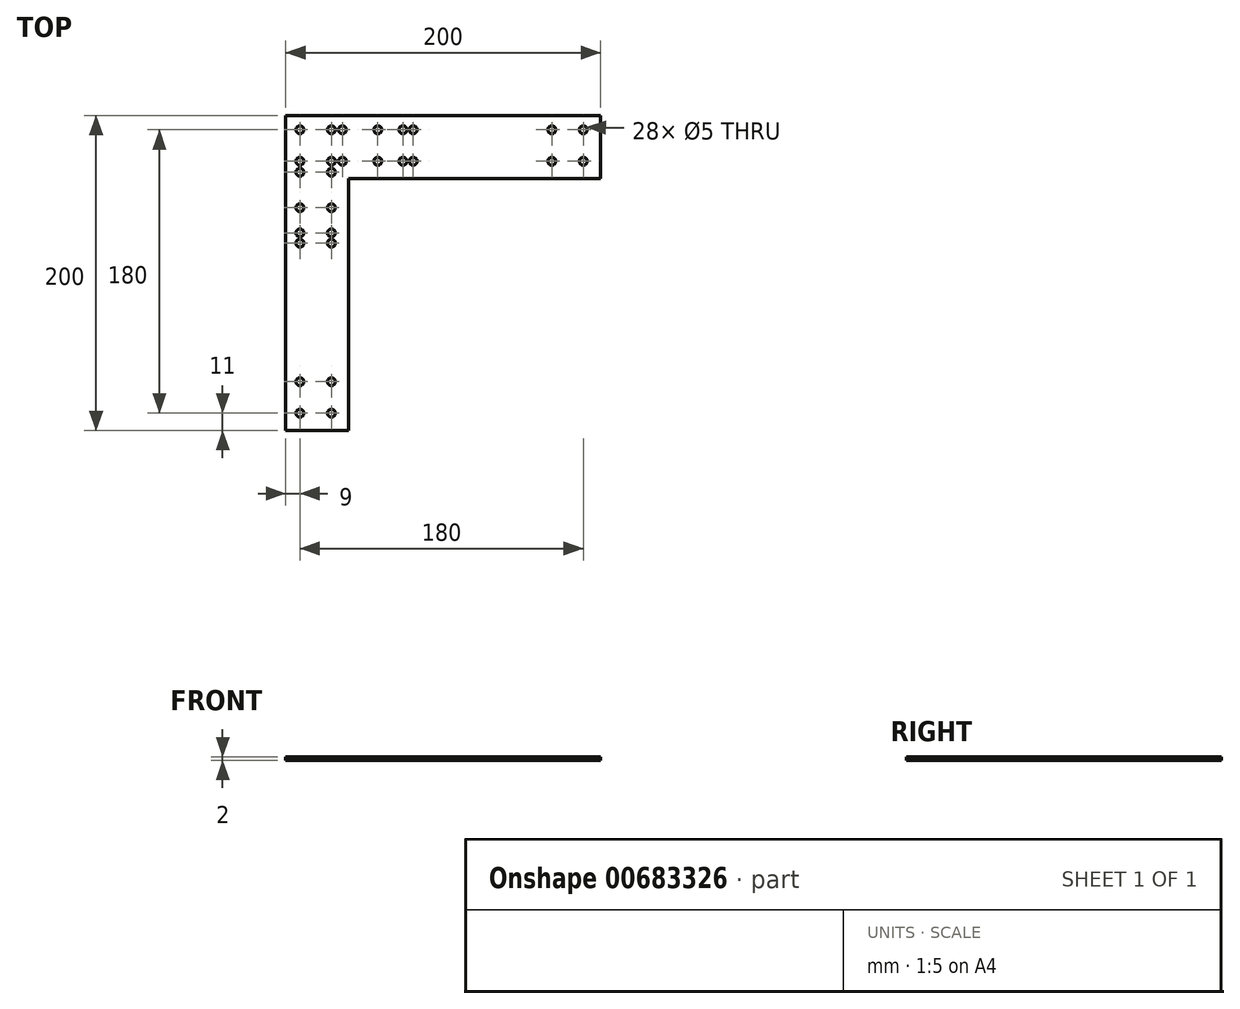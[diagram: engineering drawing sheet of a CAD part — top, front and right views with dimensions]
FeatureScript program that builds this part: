
annotation { "Feature Type Name" : "Feature", "Feature Type Description" : "" }
export const myFeature = defineFeature(function(context is Context, id is Id, definition is map)
    precondition{}
    {
        {
            var Q0;
            Q0=qCreatedBy(makeId("Top.planeOp"),FACE);
            var sketch = newSketch(context, id + "F0", { "sketchPlane" : qUnion([Q0])});
            skLineSegment(sketch, "E0", {"start": v(0, 0) * mm, "end": v(200, 0) * mm});
            skLineSegment(sketch, "E1", {"start": v(0, 0) * mm, "end": v(0, -200) * mm});
            skLineSegment(sketch, "E2.bottom", {"start": v(0, 0) * mm, "end": v(9, 0) * mm, "construction": true});
            skLineSegment(sketch, "E2.top", {"start": v(0, -9) * mm, "end": v(9, -9) * mm, "construction": true});
            skLineSegment(sketch, "E2.left", {"start": v(0, 0) * mm, "end": v(0, -9) * mm, "construction": true});
            skLineSegment(sketch, "E2.right", {"start": v(9, 0) * mm, "end": v(9, -9) * mm, "construction": true});
            skCircle(sketch, "E3", {"center": v(9, -9) * mm, "radius": 2.5 * mm});
            skLineSegment(sketch, "E4.bottom", {"start": v(9, -9) * mm, "end": v(29, -9) * mm, "construction": true});
            skLineSegment(sketch, "E4.top", {"start": v(9, -29) * mm, "end": v(29, -29) * mm, "construction": true});
            skLineSegment(sketch, "E4.left", {"start": v(9, -9) * mm, "end": v(9, -29) * mm, "construction": true});
            skLineSegment(sketch, "E4.right", {"start": v(29, -9) * mm, "end": v(29, -29) * mm, "construction": true});
            skLineSegment(sketch, "E5", {"start": v(29, -9) * mm, "end": v(169, -9) * mm, "construction": true});
            skLineSegment(sketch, "E6", {"start": v(9, -29) * mm, "end": v(9, -169) * mm, "construction": true});
            skLineSegment(sketch, "E7.bottom", {"start": v(9, -169) * mm, "end": v(29, -169) * mm, "construction": true});
            skLineSegment(sketch, "E7.top", {"start": v(9, -189) * mm, "end": v(29, -189) * mm, "construction": true});
            skLineSegment(sketch, "E7.left", {"start": v(9, -169) * mm, "end": v(9, -189) * mm, "construction": true});
            skLineSegment(sketch, "E7.right", {"start": v(29, -169) * mm, "end": v(29, -189) * mm, "construction": true});
            skLineSegment(sketch, "E8.bottom", {"start": v(169, -9) * mm, "end": v(189, -9) * mm, "construction": true});
            skLineSegment(sketch, "E8.top", {"start": v(169, -29) * mm, "end": v(189, -29) * mm, "construction": true});
            skLineSegment(sketch, "E8.left", {"start": v(169, -9) * mm, "end": v(169, -29) * mm, "construction": true});
            skLineSegment(sketch, "E8.right", {"start": v(189, -9) * mm, "end": v(189, -29) * mm, "construction": true});
            skCircle(sketch, "E9", {"center": v(169, -9) * mm, "radius": 2.5 * mm});
            skCircle(sketch, "E10", {"center": v(169, -29) * mm, "radius": 2.5 * mm});
            skCircle(sketch, "E11", {"center": v(189, -9) * mm, "radius": 2.5 * mm});
            skCircle(sketch, "E12", {"center": v(189, -29) * mm, "radius": 2.5 * mm});
            skCircle(sketch, "E13", {"center": v(29, -29) * mm, "radius": 2.5 * mm});
            skCircle(sketch, "E14", {"center": v(29, -9) * mm, "radius": 2.5 * mm});
            skCircle(sketch, "E15", {"center": v(9, -29) * mm, "radius": 2.5 * mm});
            skCircle(sketch, "E16", {"center": v(9, -169) * mm, "radius": 2.5 * mm});
            skCircle(sketch, "E17", {"center": v(29, -169) * mm, "radius": 2.5 * mm});
            skCircle(sketch, "E18", {"center": v(29, -189) * mm, "radius": 2.5 * mm});
            skCircle(sketch, "E19", {"center": v(9, -189) * mm, "radius": 2.5 * mm});
            skLineSegment(sketch, "E20.top", {"start": v(0, -40) * mm, "end": v(200, -40) * mm});
            skLineSegment(sketch, "E20.left", {"start": v(0, 0) * mm, "end": v(0, -40) * mm});
            skLineSegment(sketch, "E20.right", {"start": v(200, 0) * mm, "end": v(200, -40) * mm});
            skLineSegment(sketch, "E21.bottom", {"start": v(0, 0) * mm, "end": v(40, 0) * mm});
            skLineSegment(sketch, "E21.top", {"start": v(0, -200) * mm, "end": v(40, -200) * mm});
            skLineSegment(sketch, "E21.right", {"start": v(40, 0) * mm, "end": v(40, -200) * mm});
            skLineSegment(sketch, "E22", {"start": v(29, -29) * mm, "end": v(58.5, -29) * mm});
            skLineSegment(sketch, "E23", {"start": v(29, -29) * mm, "end": v(74.5, -29) * mm});
            skLineSegment(sketch, "E24", {"start": v(58.5, -29) * mm, "end": v(58.5, -9) * mm});
            skLineSegment(sketch, "E25", {"start": v(74.5, -29) * mm, "end": v(74.5, -9) * mm});
            skCircle(sketch, "E26", {"center": v(58.5, -9) * mm, "radius": 2.5 * mm});
            skCircle(sketch, "E27", {"center": v(74.5, -9) * mm, "radius": 2.5 * mm});
            skCircle(sketch, "E28", {"center": v(74.5, -29) * mm, "radius": 2.5 * mm});
            skCircle(sketch, "E29", {"center": v(58.5, -29) * mm, "radius": 2.5 * mm});
            skLineSegment(sketch, "E30.bottom", {"start": v(81, -9) * mm, "end": v(36, -9) * mm});
            skLineSegment(sketch, "E30.top", {"start": v(81, -29) * mm, "end": v(36, -29) * mm});
            skLineSegment(sketch, "E30.left", {"start": v(81, -9) * mm, "end": v(81, -29) * mm});
            skLineSegment(sketch, "E30.right", {"start": v(36, -9) * mm, "end": v(36, -29) * mm});
            skPoint(sketch, "E30.middle", {"position": v(58.5, -19) * mm});
            skCircle(sketch, "E31", {"center": v(81, -9) * mm, "radius": 2.5 * mm});
            skCircle(sketch, "E32", {"center": v(81, -29) * mm, "radius": 2.5 * mm});
            skCircle(sketch, "E33", {"center": v(36, -29) * mm, "radius": 2.5 * mm});
            skCircle(sketch, "E34", {"center": v(36, -9) * mm, "radius": 2.5 * mm});
            skLineSegment(sketch, "E35", {"start": v(29, -29) * mm, "end": v(29, -58.5) * mm});
            skLineSegment(sketch, "E36", {"start": v(29, -29) * mm, "end": v(29, -74.5) * mm});
            skLineSegment(sketch, "E37", {"start": v(29, -58.5) * mm, "end": v(9, -58.5) * mm});
            skLineSegment(sketch, "E38", {"start": v(29, -74.5) * mm, "end": v(9, -74.5) * mm});
            skCircle(sketch, "E39", {"center": v(9, -58.5) * mm, "radius": 2.5 * mm});
            skCircle(sketch, "E40", {"center": v(29, -58.5) * mm, "radius": 2.5 * mm});
            skCircle(sketch, "E41", {"center": v(29, -74.5) * mm, "radius": 2.5 * mm});
            skCircle(sketch, "E42", {"center": v(9, -74.5) * mm, "radius": 2.5 * mm});
            skLineSegment(sketch, "E43.bottom", {"start": v(29, -36) * mm, "end": v(9, -36) * mm});
            skLineSegment(sketch, "E43.top", {"start": v(29, -81) * mm, "end": v(9, -81) * mm});
            skLineSegment(sketch, "E43.left", {"start": v(29, -36) * mm, "end": v(29, -81) * mm});
            skLineSegment(sketch, "E43.right", {"start": v(9, -36) * mm, "end": v(9, -81) * mm});
            skPoint(sketch, "E43.middle", {"position": v(19, -58.5) * mm});
            skCircle(sketch, "E44", {"center": v(9, -36) * mm, "radius": 2.5 * mm});
            skCircle(sketch, "E45", {"center": v(9, -81) * mm, "radius": 2.5 * mm});
            skCircle(sketch, "E46", {"center": v(29, -81) * mm, "radius": 2.5 * mm});
            skCircle(sketch, "E47", {"center": v(29, -36) * mm, "radius": 2.5 * mm});
            skSolve(sketch);
        }
        {
            var Q0;
            Q0 = qSketchRegion(id + "F0", true);
            var Q1;
            {var subQ6=sQuery(id+"F0.wireOp",EDGE,"E21.right");var subQ9=sQuery(id+"F0.wireOp",EDGE,"E30.bottom");var subQ10=makeQuery(id+"F0.imprint","INTERSECT",VERTEX,{"derivedFrom":[subQ6,subQ9]});Q1=makeQuery(id+"F0.imprint","IMPRINT",FACE,{"disambiguationData":[TD([[makeQuery(id+"F0.imprint","IMPRINT",EDGE,{"disambiguationData":[TD([[subQ10,-1.0]])],"derivedFrom":subQ6}),-1.0]])]});}
            var Q2;
            {var subQ3=sQuery(id+"F0.wireOp",EDGE,"E30.bottom");var subQ9=sQuery(id+"F0.wireOp",EDGE,"E21.right");var subQ10=makeQuery(id+"F0.imprint","INTERSECT",VERTEX,{"derivedFrom":[subQ9,subQ3]});Q2=makeQuery(id+"F0.imprint","IMPRINT",FACE,{"disambiguationData":[TD([[makeQuery(id+"F0.imprint","IMPRINT",EDGE,{"disambiguationData":[TD([[subQ10,-1.0]])],"derivedFrom":subQ9}),1.0]])]});}
            var Q3;
            {var subQ0=sQuery(id+"F0.wireOp",EDGE,"E28");var subQ1=sQuery(id+"F0.wireOp",EDGE,"E25");var subQ2=makeQuery(id+"F0.imprint","INTERSECT",VERTEX,{"derivedFrom":[subQ1,subQ0]});Q3=makeQuery(id+"F0.imprint","IMPRINT",FACE,{"disambiguationData":[TD([[makeQuery(id+"F0.imprint","IMPRINT",EDGE,{"disambiguationData":[TD([[subQ2,-1.0]])],"derivedFrom":subQ1}),-1.0]])]});}
            var Q4;
            {var subQ8=sQuery(id+"F0.wireOp",EDGE,"E29");var subQ11=sQuery(id+"F0.wireOp",EDGE,"E24");var subQ15=makeQuery(id+"F0.imprint","INTERSECT",VERTEX,{"derivedFrom":[subQ11,subQ8]});Q4=makeQuery(id+"F0.imprint","IMPRINT",FACE,{"disambiguationData":[TD([[makeQuery(id+"F0.imprint","IMPRINT",EDGE,{"disambiguationData":[TD([[subQ15,-1.0]])],"derivedFrom":subQ11}),-1.0]])]});}
            var Q5;
            {var subQ6=sQuery(id+"F0.wireOp",EDGE,"E38");var subQ10=sQuery(id+"F0.wireOp",EDGE,"E41");var subQ11=makeQuery(id+"F0.imprint","INTERSECT",VERTEX,{"derivedFrom":[subQ6,subQ10]});Q5=makeQuery(id+"F0.imprint","IMPRINT",FACE,{"disambiguationData":[TD([[makeQuery(id+"F0.imprint","IMPRINT",EDGE,{"disambiguationData":[TD([[subQ11,-1.0]])],"derivedFrom":subQ6}),1.0]])]});}
            var Q6;
            {var subQ0=sQuery(id+"F0.wireOp",EDGE,"E40");var subQ1=sQuery(id+"F0.wireOp",EDGE,"E37");var subQ2=makeQuery(id+"F0.imprint","INTERSECT",VERTEX,{"derivedFrom":[subQ1,subQ0]});Q6=makeQuery(id+"F0.imprint","IMPRINT",FACE,{"disambiguationData":[TD([[makeQuery(id+"F0.imprint","IMPRINT",EDGE,{"disambiguationData":[TD([[subQ2,-1.0]])],"derivedFrom":subQ1}),1.0]])]});}
            var Q7;
            {var subQ3=sQuery(id+"F0.wireOp",EDGE,"E43.right");var subQ5=sQuery(id+"F0.wireOp",EDGE,"E20.top");var subQ6=makeQuery(id+"F0.imprint","INTERSECT",VERTEX,{"derivedFrom":[subQ5,subQ3]});Q7=makeQuery(id+"F0.imprint","IMPRINT",FACE,{"disambiguationData":[TD([[makeQuery(id+"F0.imprint","IMPRINT",EDGE,{"disambiguationData":[TD([[subQ6,-1.0]])],"derivedFrom":subQ5}),-1.0]])]});}
            var Q8;
            {var subQ0=sQuery(id+"F0.wireOp",EDGE,"E43.right");var subQ1=sQuery(id+"F0.wireOp",EDGE,"E20.top");var subQ2=makeQuery(id+"F0.imprint","INTERSECT",VERTEX,{"derivedFrom":[subQ1,subQ0]});Q8=makeQuery(id+"F0.imprint","IMPRINT",FACE,{"disambiguationData":[TD([[makeQuery(id+"F0.imprint","IMPRINT",EDGE,{"disambiguationData":[TD([[subQ2,-1.0]])],"derivedFrom":subQ1}),1.0]])]});}
            extrude(context, id + "F1", {"entities" : qUnion([Q0, Q1, Q2, Q3, Q4, Q5, Q6, Q7, Q8]), "depth" : 2 * mm, "offsetDistance" : 25 * mm});
        }
    });
